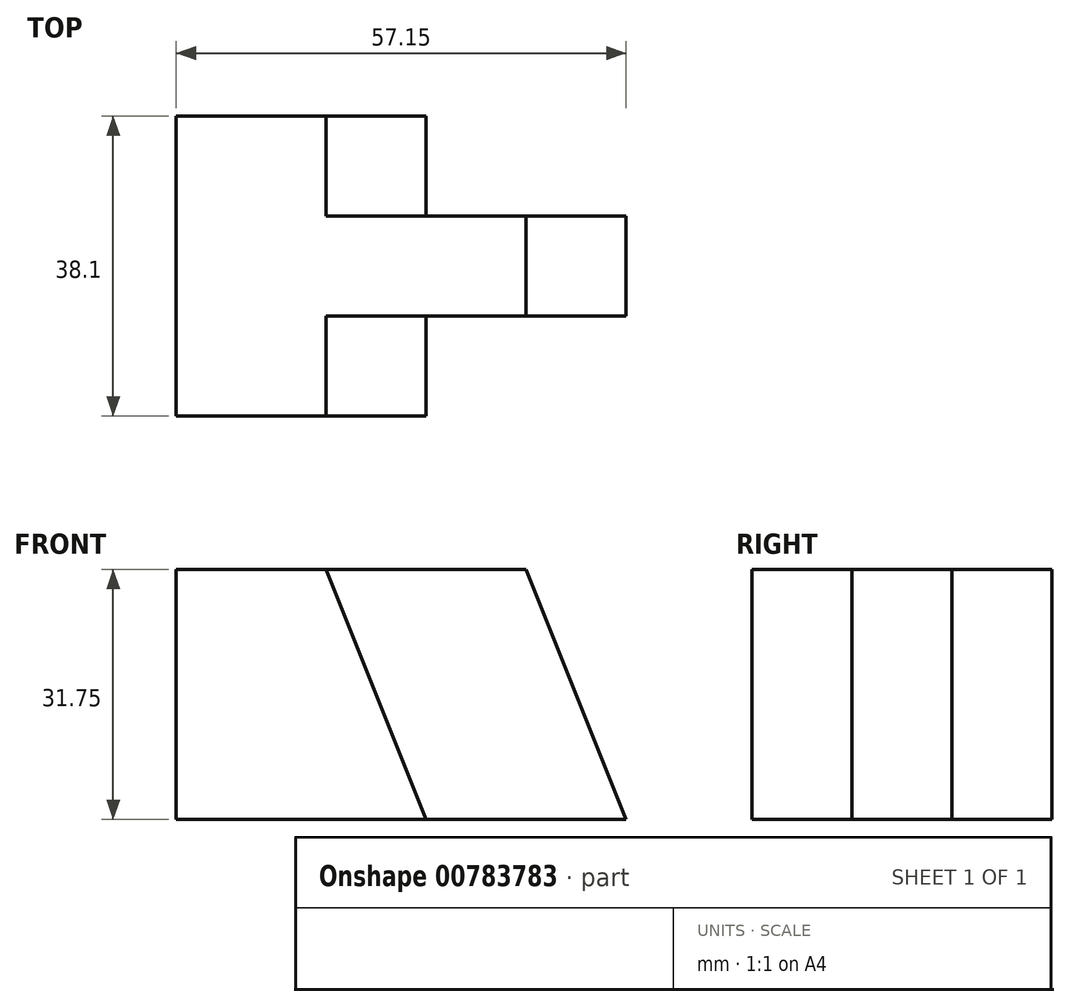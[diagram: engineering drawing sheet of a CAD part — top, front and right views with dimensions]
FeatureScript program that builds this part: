
annotation { "Feature Type Name" : "Feature", "Feature Type Description" : "" }
export const myFeature = defineFeature(function(context is Context, id is Id, definition is map)
    precondition{}
    {
        {
            var Q0;
            Q0=qCreatedBy(makeId("Front.planeOp"),FACE);
            var sketch = newSketch(context, id + "F0", { "sketchPlane" : qUnion([Q0])});
            skLineSegment(sketch, "E0", {"start": v(0, 0) * mm, "end": v(57.15, 0) * mm});
            skLineSegment(sketch, "E1", {"start": v(57.15, 0) * mm, "end": v(57.15, 31.75) * mm});
            skLineSegment(sketch, "E2", {"start": v(57.15, 31.75) * mm, "end": v(0, 31.75) * mm});
            skLineSegment(sketch, "E3", {"start": v(0, 31.75) * mm, "end": v(0, 0) * mm});
            skSolve(sketch);
        }
        {
            var Q0;
            Q0=makeQuery(id+"F0.imprint","IMPRINT",FACE,{"disambiguationData":[TD([[makeQuery(id+"F0.imprint","IMPRINT",EDGE,{"derivedFrom":sQuery(id+"F0.wireOp",EDGE,"E0")}),1.0]])]});
            extrude(context, id + "F1", {"entities" : qUnion([Q0]), "depth" : 38.1 * mm, "offsetDistance" : 25.4 * mm});
        }
        {
            var Q0;
            Q0=makeQuery(id+"F1.opExtrude","CAP_FACE",FACE,{"disambiguationData":[OSD([sQuery(id+"F0.wireOp",EDGE,"E0"),sQuery(id+"F0.wireOp",EDGE,"E1"),sQuery(id+"F0.wireOp",EDGE,"E2"),sQuery(id+"F0.wireOp",EDGE,"E3")])],"isStart":false});
            var sketch = newSketch(context, id + "F2", { "sketchPlane" : qUnion([Q0])});
            skLineSegment(sketch, "E4", {"start": v(0, 31.75) * mm, "end": v(19.05, 31.75) * mm});
            skLineSegment(sketch, "E5", {"start": v(0, 0) * mm, "end": v(31.75, 0) * mm});
            skLineSegment(sketch, "E6", {"start": v(31.75, 0) * mm, "end": v(19.05, 31.75) * mm});
            skSolve(sketch);
        }
        {
            var Q0;
            {var subQ0=sQuery(id+"F2.wireOp",EDGE,"E6");Q0=makeQuery(id+"F2.imprint","IMPRINT",FACE,{"disambiguationData":[TD([[makeQuery(id+"F2.imprint","IMPRINT",EDGE,{"derivedFrom":subQ0}),-1.0]])]});}
            extrude(context, id + "F3", {"entities" : qUnion([Q0]), "operationType" : NewBodyOperationType.REMOVE, "oppositeDirection" : true, "depth" : 12.7 * mm, "offsetDistance" : 25.4 * mm});
        }
        {
            var Q0;
            Q0=makeQuery(id+"F1.opExtrude","CAP_FACE",FACE,{"disambiguationData":[OSD([sQuery(id+"F0.wireOp",EDGE,"E0"),sQuery(id+"F0.wireOp",EDGE,"E1"),sQuery(id+"F0.wireOp",EDGE,"E2"),sQuery(id+"F0.wireOp",EDGE,"E3")])],"isStart":true});
            var sketch = newSketch(context, id + "F4", { "sketchPlane" : qUnion([Q0])});
            skLineSegment(sketch, "E7", {"start": v(0, 0) * mm, "end": v(-31.75, 0) * mm});
            skLineSegment(sketch, "E8", {"start": v(0, 31.75) * mm, "end": v(-19.05, 31.75) * mm});
            skLineSegment(sketch, "E9", {"start": v(-19.05, 31.75) * mm, "end": v(-31.75, 0) * mm});
            skSolve(sketch);
        }
        {
            var Q0;
            {var subQ0=sQuery(id+"F4.wireOp",EDGE,"E9");Q0=makeQuery(id+"F4.imprint","IMPRINT",FACE,{"disambiguationData":[TD([[makeQuery(id+"F4.imprint","IMPRINT",EDGE,{"derivedFrom":subQ0}),-1.0]])]});}
            extrude(context, id + "F5", {"entities" : qUnion([Q0]), "operationType" : NewBodyOperationType.REMOVE, "oppositeDirection" : true, "depth" : 12.7 * mm, "offsetDistance" : 25.4 * mm});
        }
        {
            var Q0;
            Q0=makeQuery(id+"F3.boolean.opBoolean","COPY",FACE,{"derivedFrom":makeQuery(id+"F3.opExtrude","CAP_FACE",FACE,{"disambiguationData":[OSD([sQuery(id+"F0.wireOp",EDGE,"E0"),sQuery(id+"F0.wireOp",EDGE,"E1"),sQuery(id+"F0.wireOp",EDGE,"E2"),sQuery(id+"F2.wireOp",EDGE,"E6")])],"isStart":false})});
            var sketch = newSketch(context, id + "F6", { "sketchPlane" : qUnion([Q0])});
            skLineSegment(sketch, "E10", {"start": v(19.05, 31.75) * mm, "end": v(44.45, 31.75) * mm});
            skLineSegment(sketch, "E11", {"start": v(44.45, 31.75) * mm, "end": v(57.15, 0) * mm});
            skSolve(sketch);
        }
        {
            var Q0;
            Q0 = qSketchRegion(id + "F6", true);
            var Q1;
            {var subQ0=sQuery(id+"F6.wireOp",EDGE,"E11");Q1=makeQuery(id+"F6.imprint","IMPRINT",FACE,{"disambiguationData":[TD([[makeQuery(id+"F6.imprint","IMPRINT",EDGE,{"derivedFrom":subQ0}),1.0]])]});}
            extrude(context, id + "F7", {"entities" : qUnion([Q0, Q1]), "operationType" : NewBodyOperationType.REMOVE, "oppositeDirection" : true, "depth" : 12.7 * mm, "offsetDistance" : 25.4 * mm});
        }
    });
